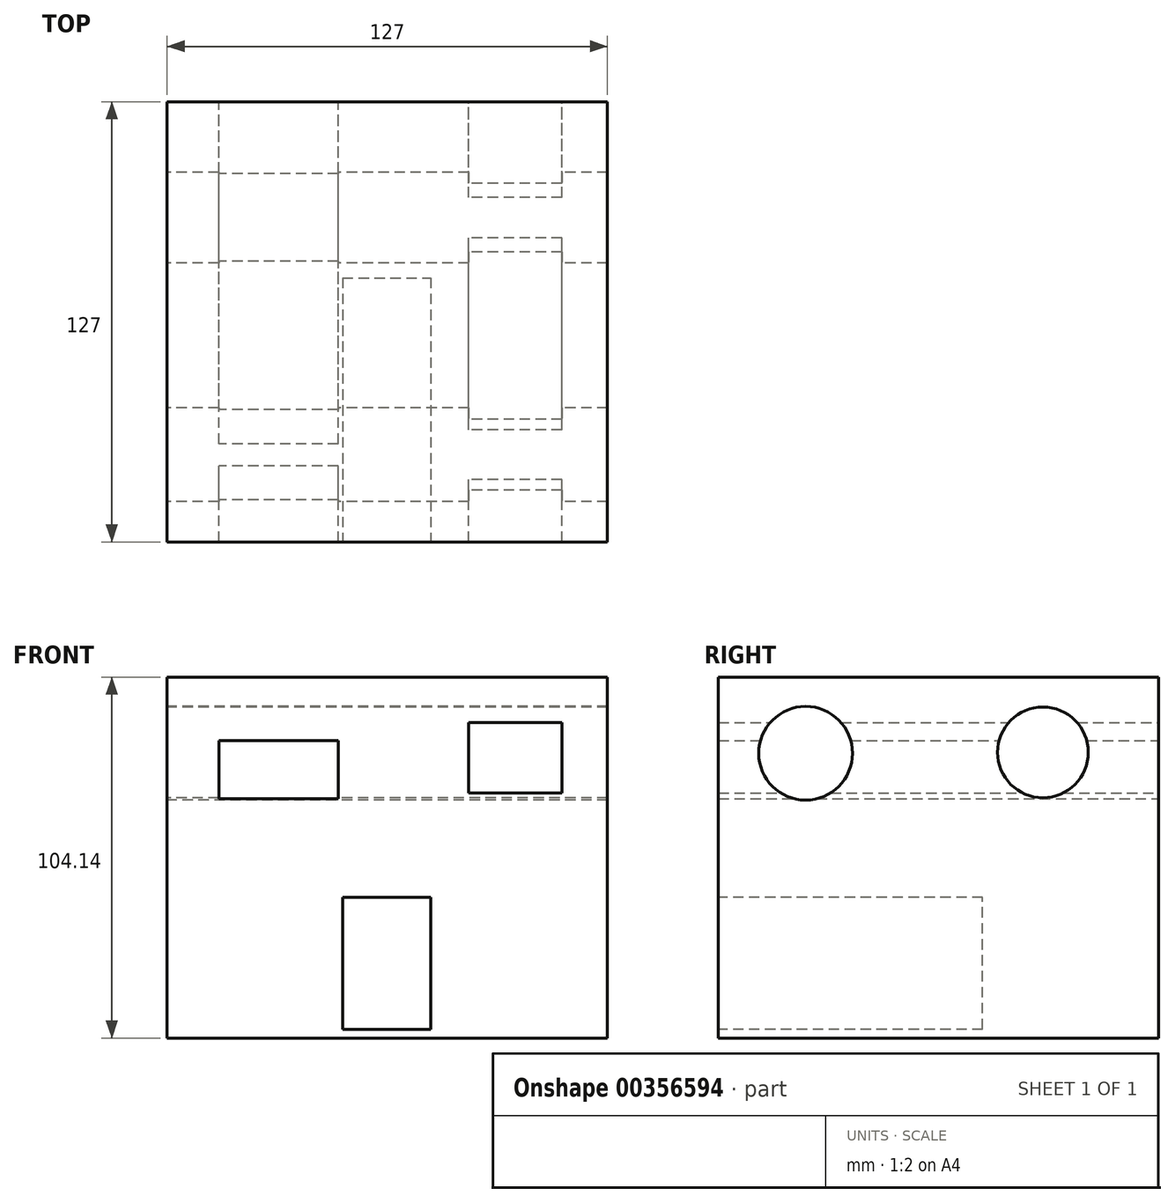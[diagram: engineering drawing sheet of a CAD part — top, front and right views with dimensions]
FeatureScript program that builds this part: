
annotation { "Feature Type Name" : "Feature", "Feature Type Description" : "" }
export const myFeature = defineFeature(function(context is Context, id is Id, definition is map)
    precondition{}
    {
        {
            var Q0;
            Q0=qCreatedBy(makeId("Top.planeOp"),FACE);
            var sketch = newSketch(context, id + "F0", { "sketchPlane" : qUnion([Q0])});
            skLineSegment(sketch, "E0.bottom", {"start": v(63.5, 63.5) * mm, "end": v(-63.5, 63.5) * mm});
            skLineSegment(sketch, "E0.top", {"start": v(63.5, -63.5) * mm, "end": v(-63.5, -63.5) * mm});
            skLineSegment(sketch, "E0.left", {"start": v(63.5, 63.5) * mm, "end": v(63.5, -63.5) * mm});
            skLineSegment(sketch, "E0.right", {"start": v(-63.5, 63.5) * mm, "end": v(-63.5, -63.5) * mm});
            skPoint(sketch, "E0.middle", {"position": v(0, 0) * mm});
            skSolve(sketch);
        }
        {
            var Q0;
            Q0 = qSketchRegion(id + "F0", true);
            extrude(context, id + "F1", {"entities" : qUnion([Q0]), "depth" : 101.6 * mm});
        }
        {
            var Q0;
            Q0=makeQuery(id+"F1.opExtrude","SWEPT_FACE",FACE,{"disambiguationData":[OSD([sQuery(id+"F0.wireOp",EDGE,"E0.top")])]});
            var sketch = newSketch(context, id + "F2", { "sketchPlane" : qUnion([Q0])});
            skLineSegment(sketch, "E1.bottom", {"start": v(-12.92, 0) * mm, "end": v(12.48, 0) * mm});
            skLineSegment(sketch, "E1.top", {"start": v(-12.92, 38.1) * mm, "end": v(12.48, 38.1) * mm});
            skLineSegment(sketch, "E1.left", {"start": v(-12.92, 0) * mm, "end": v(-12.92, 38.1) * mm});
            skLineSegment(sketch, "E1.right", {"start": v(12.48, 0) * mm, "end": v(12.48, 38.1) * mm});
            skSolve(sketch);
        }
        {
            var Q0;
            Q0 = qSketchRegion(id + "F2", true);
            extrude(context, id + "F3", {"entities" : qUnion([Q0]), "operationType" : NewBodyOperationType.REMOVE, "oppositeDirection" : true, "depth" : 76.2 * mm});
        }
        {
            var Q0;
            Q0=makeQuery(id+"F1.opExtrude","CAP_FACE",FACE,{"disambiguationData":[OSD([sQuery(id+"F0.wireOp",EDGE,"E0.bottom"),sQuery(id+"F0.wireOp",EDGE,"E0.top"),sQuery(id+"F0.wireOp",EDGE,"E0.left"),sQuery(id+"F0.wireOp",EDGE,"E0.right")])],"isStart":true});
            var sketch = newSketch(context, id + "F4", { "sketchPlane" : qUnion([Q0])});
            skLineSegment(sketch, "E2.bottom", {"start": v(-63.5, 63.5) * mm, "end": v(63.5, 63.5) * mm});
            skLineSegment(sketch, "E2.top", {"start": v(-63.5, -63.5) * mm, "end": v(63.5, -63.5) * mm});
            skLineSegment(sketch, "E2.left", {"start": v(-63.5, 63.5) * mm, "end": v(-63.5, -63.5) * mm});
            skLineSegment(sketch, "E2.right", {"start": v(63.5, 63.5) * mm, "end": v(63.5, -63.5) * mm});
            skSolve(sketch);
        }
        {
            var Q0;
            Q0 = qSketchRegion(id + "F4", true);
            extrude(context, id + "F5", {"entities" : qUnion([Q0]), "operationType" : NewBodyOperationType.ADD, "depth" : 2.54 * mm});
        }
        {
            var Q0;
            Q0=makeQuery(id+"F5.boolean.opBoolean","MERGE",FACE,{"derivedFrom":[makeQuery(id+"F1.opExtrude","SWEPT_FACE",FACE,{"disambiguationData":[OSD([sQuery(id+"F0.wireOp",EDGE,"E0.bottom")])]}),makeQuery(id+"F5.opExtrude","SWEPT_FACE",FACE,{"disambiguationData":[OSD([sQuery(id+"F4.wireOp",EDGE,"E2.top")])]})]});
            var sketch = newSketch(context, id + "F6", { "sketchPlane" : qUnion([Q0])});
            skLineSegment(sketch, "E3.bottom", {"start": v(-50.34, 88.45) * mm, "end": v(-23.46, 88.45) * mm});
            skLineSegment(sketch, "E3.top", {"start": v(-50.34, 68.17) * mm, "end": v(-23.46, 68.17) * mm});
            skLineSegment(sketch, "E3.left", {"start": v(-50.34, 88.45) * mm, "end": v(-50.34, 68.17) * mm});
            skLineSegment(sketch, "E3.right", {"start": v(-23.46, 88.45) * mm, "end": v(-23.46, 68.17) * mm});
            skLineSegment(sketch, "E4.bottom", {"start": v(14.17, 83.32) * mm, "end": v(48.63, 83.32) * mm});
            skLineSegment(sketch, "E4.top", {"start": v(14.17, 66.46) * mm, "end": v(48.63, 66.46) * mm});
            skLineSegment(sketch, "E4.left", {"start": v(14.17, 83.32) * mm, "end": v(14.17, 66.46) * mm});
            skLineSegment(sketch, "E4.right", {"start": v(48.63, 83.32) * mm, "end": v(48.63, 66.46) * mm});
            skSolve(sketch);
        }
        {
            var Q0;
            Q0=makeQuery(id+"F6.imprint","IMPRINT",FACE,{"disambiguationData":[TD([[makeQuery(id+"F6.imprint","IMPRINT",EDGE,{"derivedFrom":sQuery(id+"F6.wireOp",EDGE,"E4.bottom")}),-1.0]])]});
            var Q1;
            Q1=makeQuery(id+"F6.imprint","IMPRINT",FACE,{"disambiguationData":[TD([[makeQuery(id+"F6.imprint","IMPRINT",EDGE,{"derivedFrom":sQuery(id+"F6.wireOp",EDGE,"E3.bottom")}),-1.0]])]});
            extrude(context, id + "F7", {"entities" : qUnion([Q0, Q1]), "operationType" : NewBodyOperationType.REMOVE, "endBound" : BoundingType.THROUGH_ALL, "oppositeDirection" : true, "depth" : 25.4 * mm});
        }
        {
            var Q0;
            Q0=makeQuery(id+"F5.boolean.opBoolean","MERGE",FACE,{"derivedFrom":[makeQuery(id+"F1.opExtrude","SWEPT_FACE",FACE,{"disambiguationData":[OSD([sQuery(id+"F0.wireOp",EDGE,"E0.right")])]}),makeQuery(id+"F5.opExtrude","SWEPT_FACE",FACE,{"disambiguationData":[OSD([sQuery(id+"F4.wireOp",EDGE,"E2.left")])]})]});
            var sketch = newSketch(context, id + "F8", { "sketchPlane" : qUnion([Q0])});
            skCircle(sketch, "E5", {"center": v(-30.07, 79.87) * mm, "radius": 13.1 * mm});
            skPoint(sketch, "E5.first.point", {"position": v(-42.76, 83.08) * mm});
            skPoint(sketch, "E5.second.point", {"position": v(-17.84, 84.54) * mm});
            skPoint(sketch, "E5.third.point", {"position": v(-19.55, 72.08) * mm});
            skCircle(sketch, "E6", {"center": v(38.37, 79.6) * mm, "radius": 13.52 * mm});
            skPoint(sketch, "E6.first.point", {"position": v(28.83, 89.18) * mm});
            skPoint(sketch, "E6.second.point", {"position": v(49.6, 72.08) * mm});
            skPoint(sketch, "E6.third.point", {"position": v(25.41, 75.74) * mm});
            skSolve(sketch);
        }
        {
            var Q0;
            Q0=makeQuery(id+"F8.imprint","IMPRINT",FACE,{"disambiguationData":[TD([[makeQuery(id+"F8.imprint","IMPRINT",EDGE,{"derivedFrom":sQuery(id+"F8.wireOp",EDGE,"E5")}),1.0]])]});
            var Q1;
            Q1=makeQuery(id+"F8.imprint","IMPRINT",FACE,{"disambiguationData":[TD([[makeQuery(id+"F8.imprint","IMPRINT",EDGE,{"derivedFrom":sQuery(id+"F8.wireOp",EDGE,"E6")}),1.0]])]});
            extrude(context, id + "F9", {"entities" : qUnion([Q0, Q1]), "operationType" : NewBodyOperationType.REMOVE, "endBound" : BoundingType.THROUGH_ALL, "oppositeDirection" : true, "depth" : 25.4 * mm});
        }
    });
